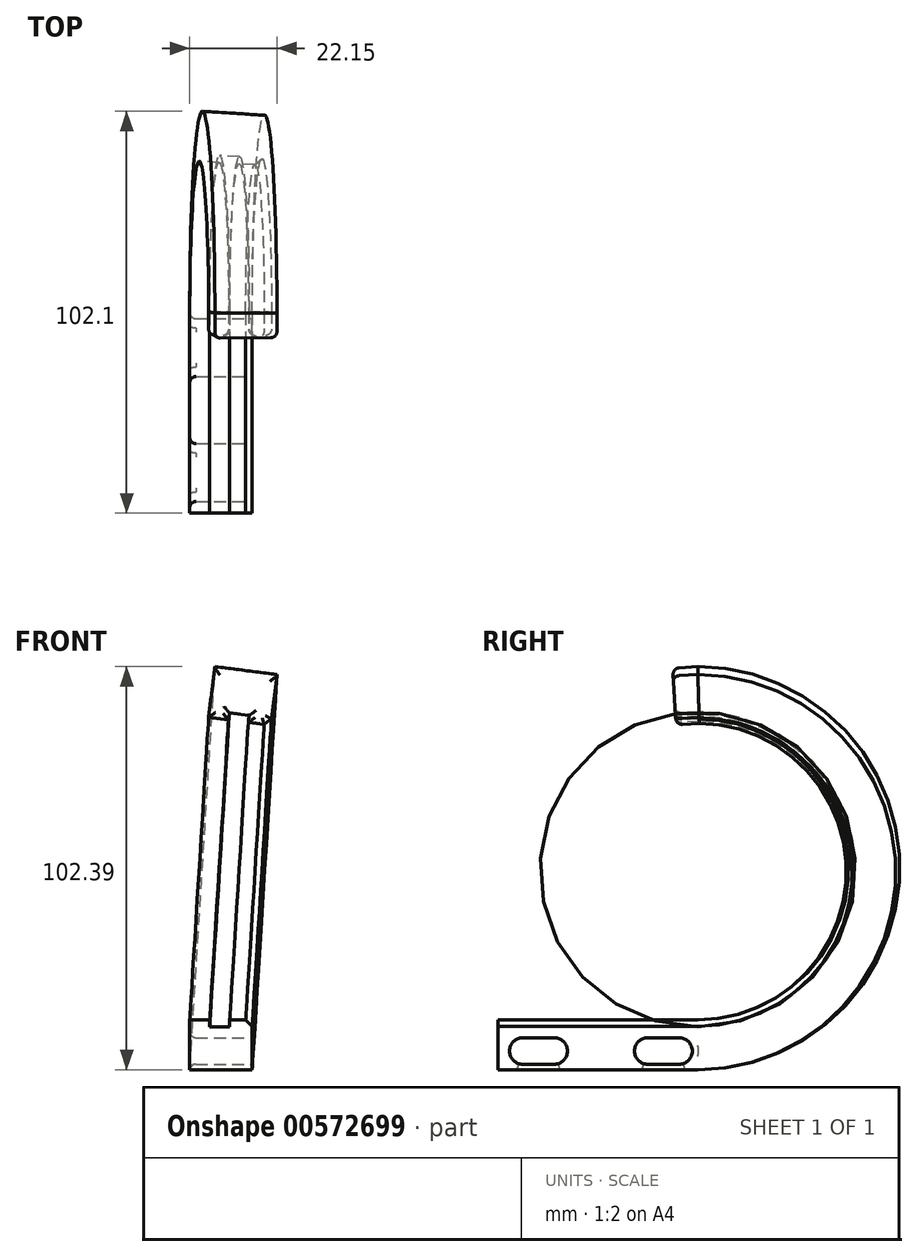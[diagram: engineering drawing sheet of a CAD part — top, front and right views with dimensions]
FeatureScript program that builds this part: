
annotation { "Feature Type Name" : "Feature", "Feature Type Description" : "" }
export const myFeature = defineFeature(function(context is Context, id is Id, definition is map)
    precondition{}
    {
        {
            var Q0;
            Q0=qCreatedBy(makeId("Front.planeOp"),FACE);
            var sketch = newSketch(context, id + "F0", { "sketchPlane" : qUnion([Q0])});
            skLineSegment(sketch, "E0", {"start": v(0, 0) * mm, "end": v(7.94, 0) * mm});
            skLineSegment(sketch, "E1", {"start": v(6.29, 12.7) * mm, "end": v(2.22, 12.7) * mm});
            skLineSegment(sketch, "E2", {"start": v(2.22, 12.7) * mm, "end": v(2.22, 10.92) * mm});
            skLineSegment(sketch, "E3", {"start": v(2.22, 10.92) * mm, "end": v(-2.86, 10.92) * mm});
            skLineSegment(sketch, "E4", {"start": v(-2.86, 10.92) * mm, "end": v(-2.86, 12.7) * mm});
            skLineSegment(sketch, "E5", {"start": v(-2.86, 12.7) * mm, "end": v(-7.94, 12.7) * mm});
            skLineSegment(sketch, "E6", {"start": v(-7.94, 12.7) * mm, "end": v(-7.94, 0) * mm});
            skLineSegment(sketch, "E7", {"start": v(-7.94, 0) * mm, "end": v(0, 0) * mm});
            skLineSegment(sketch, "E8", {"start": v(6.29, 12.7) * mm, "end": v(7.94, 11.05) * mm});
            skLineSegment(sketch, "E9", {"start": v(7.94, 0) * mm, "end": v(7.94, 11.05) * mm});
            skSolve(sketch);
        }
        {
            var Q0;
            Q0=qCreatedBy(makeId("Right.planeOp"),FACE);
            var sketch = newSketch(context, id + "F1", { "sketchPlane" : qUnion([Q0])});
            skLineSegment(sketch, "E10", {"start": v(-50.8, 0) * mm, "end": v(0, 0) * mm});
            skSolve(sketch);
        }
        {
            var Q0;
            Q0 = qSketchRegion(id + "F0", true);
            var Q1;
            Q1 = qConstructionFilter(qBodyType(qCreatedBy(id + "F1" ,EDGE), BodyType.WIRE), ConstructionObject.NO);
            sweep(context, id + "F2", {"profiles" : qUnion([Q0]), "path" : qUnion([Q1])});
        }
        {
            var Q0;
            Q0=qCreatedBy(makeId("Top.planeOp"),FACE);
            var sketch = newSketch(context, id + "F3", { "sketchPlane" : qUnion([Q0])});
            skLineSegment(sketch, "E11", {"start": v(0, 0) * mm, "end": v(0, 11.8) * mm});
            skSolve(sketch);
        }
        {
            var Q0;
            Q0 = qBodyType(qCreatedBy(id + "F3" ,EDGE), BodyType.WIRE);
            cPlane(context, id + "F4", {"entities" : qUnion([Q0]), "cplaneType" : CPlaneType.LINE_ANGLE, "offset" : 25.4 * mm, "angle" : 93.58 * degree, "width" : 152.4 * mm, "height" : 152.4 * mm});
        }
        {
            var Q0;
            Q0=qCreatedBy(id+"F4.planeOp",FACE);
            var sketch = newSketch(context, id + "F5", { "sketchPlane" : qUnion([Q0])});
            skLineSegment(sketch, "E12", {"start": v(0, 0) * mm, "end": v(0, -18.52) * mm});
            skArc(sketch, "E13", {"start": v(0, 0) * mm, "mid": v(50.8, 50.8) * mm, "end": v(0, 101.6) * mm});
            skFitSpline(sketch, "E14", {"points": [v(0, 101.6) * mm, v(-6.35, 101.2) * mm], "startDerivative": vector(-6.35, -0.4) * mm, "endDerivative": vector(-6.35, -0.4) * mm});
            skSolve(sketch);
        }
        {
            var Q0;
            Q0=makeQuery(id+"F2.opSweep","CAP_FACE",FACE,{"disambiguationData":[OSD([sQuery(id+"F0.wireOp",EDGE,"E0"),sQuery(id+"F0.wireOp",EDGE,"E1"),sQuery(id+"F0.wireOp",EDGE,"E2"),sQuery(id+"F0.wireOp",EDGE,"E3"),sQuery(id+"F0.wireOp",EDGE,"E4"),sQuery(id+"F0.wireOp",EDGE,"E5"),sQuery(id+"F0.wireOp",EDGE,"E6"),sQuery(id+"F0.wireOp",EDGE,"E7"),sQuery(id+"F0.wireOp",EDGE,"E8"),sQuery(id+"F0.wireOp",EDGE,"E9"),sQuery(id+"F1.wireOp",VERTEX,"E10.start")])],"isStart":true});
            var Q1;
            Q1=sQuery(id+"F5.wireOp",EDGE,"E13");
            var Q2;
            Q2=sQuery(id+"F5.wireOp",EDGE,"E14");
            sweep(context, id + "F6", {"operationType" : NewBodyOperationType.ADD, "profiles" : qUnion([Q0]), "path" : qUnion([Q1, Q2])});
        }
        {
            var Q0;
            Q0=makeQuery(id+"F2.opSweep","SWEPT_FACE",FACE,{"disambiguationData":[OSD([sQuery(id+"F0.wireOp",EDGE,"E9"),sQuery(id+"F1.wireOp",EDGE,"E10")])]});
            var sketch = newSketch(context, id + "F7", { "sketchPlane" : qUnion([Q0])});
            skLineSegment(sketch, "E15", {"start": v(-50.8, 0) * mm, "end": v(-50.8, 4.75) * mm});
            skLineSegment(sketch, "E16", {"start": v(-50.8, 4.75) * mm, "end": v(-44.45, 4.75) * mm});
            skLineSegment(sketch, "E17", {"start": v(-44.45, 4.75) * mm, "end": v(-40.48, 4.75) * mm});
            skLineSegment(sketch, "E18", {"start": v(-44.45, 4.75) * mm, "end": v(-47.82, 4.75) * mm});
            skLineSegment(sketch, "E19", {"start": v(-44.45, 4.75) * mm, "end": v(-44.45, 8.12) * mm});
            skLineSegment(sketch, "E20", {"start": v(-44.45, 8.12) * mm, "end": v(-44.45, 4.75) * mm});
            skLineSegment(sketch, "E21.MirrorCS", {"start": v(-44.45, 1.38) * mm, "end": v(-44.45, 4.75) * mm});
            skArc(sketch, "E22", {"start": v(-44.45, 8.12) * mm, "mid": v(-47.82, 4.75) * mm, "end": v(-44.45, 1.38) * mm});
            skLineSegment(sketch, "E23", {"start": v(-40.48, 4.75) * mm, "end": v(-40.48, 5.87) * mm});
            skArc(sketch, "E24.MirrorCS", {"start": v(-36.51, 8.12) * mm, "mid": v(-33.14, 4.75) * mm, "end": v(-36.51, 1.38) * mm});
            skLineSegment(sketch, "E25", {"start": v(-44.45, 8.12) * mm, "end": v(-36.51, 8.12) * mm});
            skLineSegment(sketch, "E26", {"start": v(-44.45, 1.38) * mm, "end": v(-36.51, 1.38) * mm});
            skLineSegment(sketch, "E27", {"start": v(-33.14, 4.75) * mm, "end": v(-24.6, 4.75) * mm});
            skPoint(sketch, "E27.endSnap0", {"position": v(-33.14, 4.75) * mm});
            skLineSegment(sketch, "E28", {"start": v(-24.6, 4.75) * mm, "end": v(-24.6, 6.48) * mm});
            skArc(sketch, "E29.MirrorCS", {"start": v(-12.7, 8.12) * mm, "mid": v(-16.08, 4.75) * mm, "end": v(-12.7, 1.38) * mm});
            skLineSegment(sketch, "E30.MirrorCS", {"start": v(-4.76, 8.12) * mm, "end": v(-12.7, 8.12) * mm});
            skLineSegment(sketch, "E31.MirrorCS", {"start": v(-4.76, 1.38) * mm, "end": v(-12.7, 1.38) * mm});
            skArc(sketch, "E32.MirrorCS", {"start": v(-4.76, 8.12) * mm, "mid": v(-1.4, 4.75) * mm, "end": v(-4.76, 1.38) * mm});
            skSolve(sketch);
        }
        {
            var Q0;
            Q0 = qSketchRegion(id + "F7", true);
            extrude(context, id + "F8", {"entities" : qUnion([Q0]), "operationType" : NewBodyOperationType.REMOVE, "endBound" : BoundingType.THROUGH_ALL, "oppositeDirection" : true, "depth" : 25.4 * mm, "offsetDistance" : 25.4 * mm});
        }
        {
            var Q0;
            Q0=makeQuery(id+"F8.boolean.opBoolean","COPY",EDGE,{"derivedFrom":makeQuery(id+"F8.opExtrude","CAP_EDGE",EDGE,{"disambiguationData":[OSD([sQuery(id+"F7.wireOp",EDGE,"E25")])],"isStart":true})});
            var Q1;
            Q1=makeQuery(id+"F8.boolean.opBoolean","COPY",EDGE,{"derivedFrom":makeQuery(id+"F8.opExtrude","CAP_EDGE",EDGE,{"disambiguationData":[OSD([sQuery(id+"F7.wireOp",EDGE,"E30.MirrorCS")])],"isStart":true})});
            var Q2;
            Q2=makeQuery(id+"F8.boolean.opBoolean","INTERSECT",EDGE,{"derivedFrom":[makeQuery(id+"F2.opSweep","SWEPT_FACE",FACE,{"disambiguationData":[OSD([sQuery(id+"F0.wireOp",EDGE,"E6"),sQuery(id+"F1.wireOp",EDGE,"E10")])]}),makeQuery(id+"F8.opExtrude","SWEPT_FACE",FACE,{"disambiguationData":[OSD([sQuery(id+"F7.wireOp",EDGE,"E30.MirrorCS")])]})]});
            var Q3;
            Q3=makeQuery(id+"F8.boolean.opBoolean","INTERSECT",EDGE,{"derivedFrom":[makeQuery(id+"F2.opSweep","SWEPT_FACE",FACE,{"disambiguationData":[OSD([sQuery(id+"F0.wireOp",EDGE,"E6"),sQuery(id+"F1.wireOp",EDGE,"E10")])]}),makeQuery(id+"F8.opExtrude","SWEPT_FACE",FACE,{"disambiguationData":[OSD([sQuery(id+"F7.wireOp",EDGE,"E25")])]})]});
            fillet(context, id + "F9", {"entities" : qUnion([Q0, Q1, Q2, Q3]), "radius" : 1.59 * mm, "tangentPropagation" : true, "allowEdgeOverflow" : false});
        }
        {
            var Q0;
            Q0=makeQuery(id+"F6.opSweep","CAP_EDGE",EDGE,{"disambiguationData":[OSD([sQuery(id+"F0.wireOp",EDGE,"E3"),sQuery(id+"F1.wireOp",VERTEX,"E10.start"),sQuery(id+"F5.wireOp",VERTEX,"E14.end")])],"isStart":false});
            var Q1;
            Q1=makeQuery(id+"F6.opSweep","CAP_EDGE",EDGE,{"disambiguationData":[OSD([sQuery(id+"F0.wireOp",EDGE,"E4"),sQuery(id+"F1.wireOp",VERTEX,"E10.start"),sQuery(id+"F5.wireOp",VERTEX,"E14.end")])],"isStart":false});
            var Q2;
            Q2=makeQuery(id+"F6.opSweep","CAP_FACE",FACE,{"disambiguationData":[OSD([sQuery(id+"F0.wireOp",EDGE,"E0"),sQuery(id+"F0.wireOp",EDGE,"E1"),sQuery(id+"F0.wireOp",EDGE,"E2"),sQuery(id+"F0.wireOp",EDGE,"E3"),sQuery(id+"F0.wireOp",EDGE,"E4"),sQuery(id+"F0.wireOp",EDGE,"E5"),sQuery(id+"F0.wireOp",EDGE,"E6"),sQuery(id+"F0.wireOp",EDGE,"E7"),sQuery(id+"F0.wireOp",EDGE,"E8"),sQuery(id+"F0.wireOp",EDGE,"E9"),sQuery(id+"F1.wireOp",VERTEX,"E10.start"),sQuery(id+"F5.wireOp",VERTEX,"E14.end")])],"isStart":false});
            fillet(context, id + "F10", {"entities" : qUnion([Q0, Q1, Q2]), "radius" : 1.59 * mm, "tangentPropagation" : true, "allowEdgeOverflow" : false});
        }
    });
